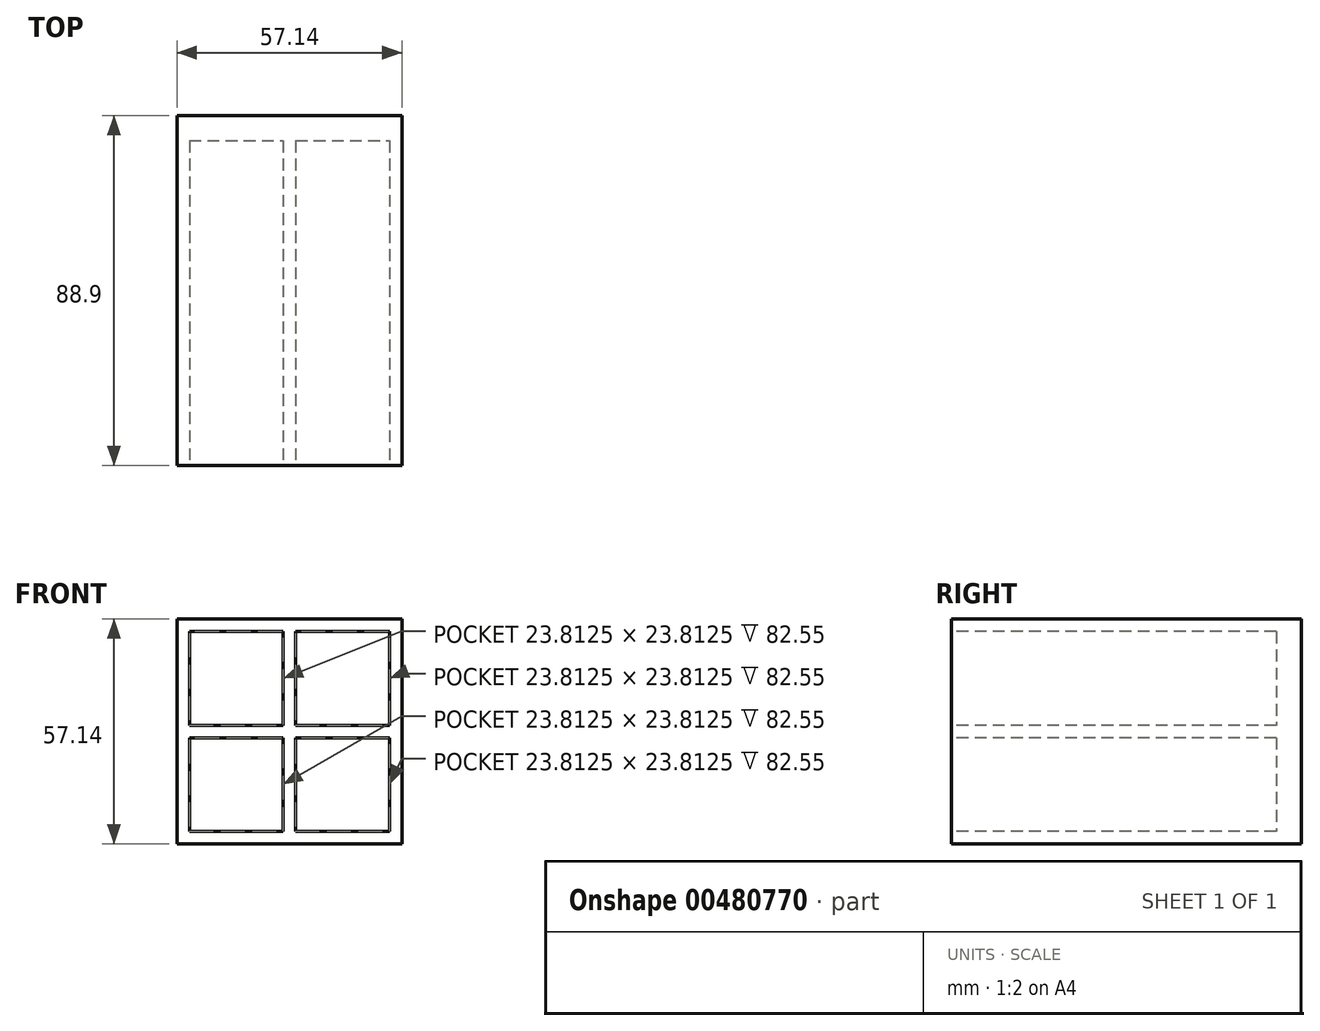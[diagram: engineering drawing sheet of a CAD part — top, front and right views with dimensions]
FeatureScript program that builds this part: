
annotation { "Feature Type Name" : "Feature", "Feature Type Description" : "" }
export const myFeature = defineFeature(function(context is Context, id is Id, definition is map)
    precondition{}
    {
        {
            var Q0;
            Q0=qCreatedBy(makeId("Front.planeOp"),FACE);
            var sketch = newSketch(context, id + "F0", { "sketchPlane" : qUnion([Q0])});
            skLineSegment(sketch, "E0.bottom", {"start": v(28.57, 28.58) * mm, "end": v(-28.58, 28.58) * mm});
            skLineSegment(sketch, "E0.top", {"start": v(28.58, -28.58) * mm, "end": v(-28.57, -28.58) * mm});
            skLineSegment(sketch, "E0.left", {"start": v(28.57, 28.58) * mm, "end": v(28.58, -28.58) * mm});
            skLineSegment(sketch, "E0.right", {"start": v(-28.58, 28.58) * mm, "end": v(-28.57, -28.58) * mm});
            skPoint(sketch, "E0.middle", {"position": v(0, 0) * mm});
            skSolve(sketch);
        }
        {
            var Q0;
            Q0 = qSketchRegion(id + "F0", true);
            extrude(context, id + "F1", {"entities" : qUnion([Q0]), "depth" : 88.9 * mm});
        }
        {
            var Q0;
            Q0=makeQuery(id+"F1.opExtrude","CAP_FACE",FACE,{"disambiguationData":[OSD([sQuery(id+"F0.wireOp",EDGE,"E0.bottom"),sQuery(id+"F0.wireOp",EDGE,"E0.top"),sQuery(id+"F0.wireOp",EDGE,"E0.left"),sQuery(id+"F0.wireOp",EDGE,"E0.right")])],"isStart":false});
            var sketch = newSketch(context, id + "F2", { "sketchPlane" : qUnion([Q0])});
            skLineSegment(sketch, "E1.bottom", {"start": v(-25.4, 25.4) * mm, "end": v(-1.59, 25.4) * mm});
            skLineSegment(sketch, "E1.top", {"start": v(-25.4, 1.59) * mm, "end": v(-1.59, 1.59) * mm});
            skLineSegment(sketch, "E1.left", {"start": v(-25.4, 25.4) * mm, "end": v(-25.4, 1.59) * mm});
            skLineSegment(sketch, "E1.right", {"start": v(-1.59, 25.4) * mm, "end": v(-1.59, 1.59) * mm});
            skSolve(sketch);
        }
        {
            var Q0;
            Q0 = qSketchRegion(id + "F2", true);
            extrude(context, id + "F3", {"entities" : qUnion([Q0]), "operationType" : NewBodyOperationType.REMOVE, "oppositeDirection" : true, "depth" : 82.55 * mm});
        }
        {
            var Q0;
            Q0=makeQuery(id+"F1.opExtrude","CAP_FACE",FACE,{"disambiguationData":[OSD([sQuery(id+"F0.wireOp",EDGE,"E0.bottom"),sQuery(id+"F0.wireOp",EDGE,"E0.top"),sQuery(id+"F0.wireOp",EDGE,"E0.left"),sQuery(id+"F0.wireOp",EDGE,"E0.right")])],"isStart":false});
            var sketch = newSketch(context, id + "F4", { "sketchPlane" : qUnion([Q0])});
            skLineSegment(sketch, "E2.bottom", {"start": v(1.59, 25.4) * mm, "end": v(25.4, 25.4) * mm});
            skLineSegment(sketch, "E2.top", {"start": v(1.59, 1.59) * mm, "end": v(25.4, 1.59) * mm});
            skLineSegment(sketch, "E2.left", {"start": v(1.59, 25.4) * mm, "end": v(1.59, 1.59) * mm});
            skLineSegment(sketch, "E2.right", {"start": v(25.4, 25.4) * mm, "end": v(25.4, 1.59) * mm});
            skSolve(sketch);
        }
        {
            var Q0;
            Q0 = qSketchRegion(id + "F4", true);
            extrude(context, id + "F5", {"entities" : qUnion([Q0]), "operationType" : NewBodyOperationType.REMOVE, "oppositeDirection" : true, "depth" : 82.55 * mm});
        }
        {
            var Q0;
            Q0=makeQuery(id+"F1.opExtrude","CAP_FACE",FACE,{"disambiguationData":[OSD([sQuery(id+"F0.wireOp",EDGE,"E0.bottom"),sQuery(id+"F0.wireOp",EDGE,"E0.top"),sQuery(id+"F0.wireOp",EDGE,"E0.left"),sQuery(id+"F0.wireOp",EDGE,"E0.right")])],"isStart":false});
            var sketch = newSketch(context, id + "F6", { "sketchPlane" : qUnion([Q0])});
            skLineSegment(sketch, "E3.bottom", {"start": v(-25.4, -1.59) * mm, "end": v(-1.59, -1.59) * mm});
            skLineSegment(sketch, "E3.top", {"start": v(-25.4, -25.4) * mm, "end": v(-1.59, -25.4) * mm});
            skLineSegment(sketch, "E3.left", {"start": v(-25.4, -1.59) * mm, "end": v(-25.4, -25.4) * mm});
            skLineSegment(sketch, "E3.right", {"start": v(-1.59, -1.59) * mm, "end": v(-1.59, -25.4) * mm});
            skSolve(sketch);
        }
        {
            var Q0;
            Q0 = qSketchRegion(id + "F6", true);
            extrude(context, id + "F7", {"entities" : qUnion([Q0]), "operationType" : NewBodyOperationType.REMOVE, "oppositeDirection" : true, "depth" : 82.55 * mm});
        }
        {
            var Q0;
            Q0=makeQuery(id+"F1.opExtrude","CAP_FACE",FACE,{"disambiguationData":[OSD([sQuery(id+"F0.wireOp",EDGE,"E0.bottom"),sQuery(id+"F0.wireOp",EDGE,"E0.top"),sQuery(id+"F0.wireOp",EDGE,"E0.left"),sQuery(id+"F0.wireOp",EDGE,"E0.right")])],"isStart":false});
            var sketch = newSketch(context, id + "F8", { "sketchPlane" : qUnion([Q0])});
            skLineSegment(sketch, "E4.bottom", {"start": v(1.59, -1.59) * mm, "end": v(25.4, -1.59) * mm});
            skLineSegment(sketch, "E4.top", {"start": v(1.59, -25.4) * mm, "end": v(25.4, -25.4) * mm});
            skLineSegment(sketch, "E4.left", {"start": v(1.59, -1.59) * mm, "end": v(1.59, -25.4) * mm});
            skLineSegment(sketch, "E4.right", {"start": v(25.4, -1.59) * mm, "end": v(25.4, -25.4) * mm});
            skSolve(sketch);
        }
        {
            var Q0;
            Q0 = qSketchRegion(id + "F8", true);
            extrude(context, id + "F9", {"entities" : qUnion([Q0]), "operationType" : NewBodyOperationType.REMOVE, "oppositeDirection" : true, "depth" : 82.55 * mm});
        }
    });
